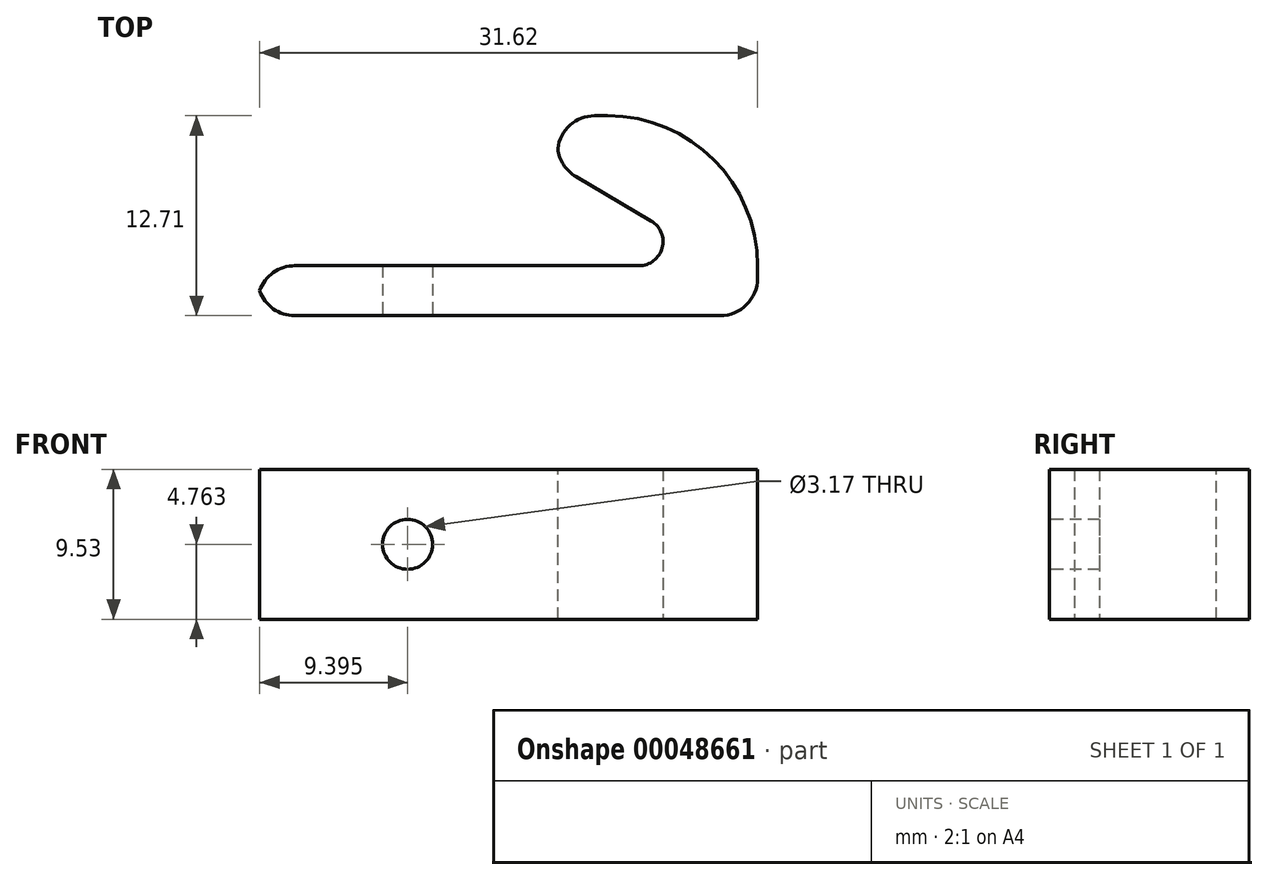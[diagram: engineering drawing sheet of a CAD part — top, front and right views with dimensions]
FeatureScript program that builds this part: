
annotation { "Feature Type Name" : "Feature", "Feature Type Description" : "" }
export const myFeature = defineFeature(function(context is Context, id is Id, definition is map)
    precondition{}
    {
        {
            var Q0;
            Q0=qCreatedBy(makeId("Top.planeOp"),FACE);
            var sketch = newSketch(context, id + "F0", { "sketchPlane" : qUnion([Q0])});
            skLineSegment(sketch, "E0.bottom", {"start": v(0, 0) * mm, "end": v(24.22, 0) * mm});
            skLineSegment(sketch, "E0.top", {"start": v(0, -3.18) * mm, "end": v(31.75, -3.18) * mm});
            skLineSegment(sketch, "E0.left", {"start": v(0, 0) * mm, "end": v(0, -3.18) * mm});
            skLineSegment(sketch, "E0.right", {"start": v(31.75, 0) * mm, "end": v(31.75, -3.18) * mm});
            skLineSegment(sketch, "E1.bottom", {"start": v(31.75, 0) * mm, "end": v(19.05, 3.17) * mm});
            skLineSegment(sketch, "E1.top", {"start": v(22.23, 9.52) * mm, "end": v(19.05, 9.52) * mm});
            skLineSegment(sketch, "E1.left", {"start": v(31.75, 0) * mm, "end": v(31.75, 0) * mm});
            skLineSegment(sketch, "E1.right", {"start": v(19.05, 6.35) * mm, "end": v(19.05, 9.52) * mm});
            skLineSegment(sketch, "E2", {"start": v(19.05, 6.35) * mm, "end": v(25, 2.84) * mm});
            skPoint(sketch, "E3.newPointA", {"position": v(31.75, 0) * mm});
            skPoint(sketch, "E3.newPointB", {"position": v(27, 1.65) * mm});
            skArc(sketch, "E3.filletArc", {"start": v(24.22, 0) * mm, "mid": v(25.7, 1.12) * mm, "end": v(25, 2.84) * mm});
            skPoint(sketch, "E4.visualSharp", {"position": v(31.75, 9.52) * mm});
            skArc(sketch, "E4.filletArc", {"start": v(31.75, 0) * mm, "mid": v(28.96, 6.74) * mm, "end": v(22.23, 9.52) * mm});
            skSolve(sketch);
        }
        {
            var Q0;
            Q0 = qSketchRegion(id + "F0", true);
            extrude(context, id + "F1", {"entities" : qUnion([Q0]), "depth" : 9.52 * mm});
        }
        {
            var Q0;
            Q0=makeQuery(id+"F1.opExtrude","SWEPT_FACE",FACE,{"disambiguationData":[OSD([sQuery(id+"F0.wireOp",EDGE,"E0.top")])]});
            var sketch = newSketch(context, id + "F2", { "sketchPlane" : qUnion([Q0])});
            skLineSegment(sketch, "E5", {"start": v(0, 4.76) * mm, "end": v(31.75, 4.76) * mm, "construction": true});
            skPoint(sketch, "E6", {"position": v(9.53, 4.76) * mm});
            skCircle(sketch, "E7", {"center": v(9.53, 4.76) * mm, "radius": 1.59 * mm});
            skSolve(sketch);
        }
        {
            var Q0;
            Q0 = qSketchRegion(id + "F2", true);
            extrude(context, id + "F3", {"entities" : qUnion([Q0]), "operationType" : NewBodyOperationType.REMOVE, "endBound" : BoundingType.THROUGH_ALL, "oppositeDirection" : true, "depth" : 25.4 * mm});
        }
        {
            var Q0;
            Q0=makeQuery(id+"F1.opExtrude","SWEPT_EDGE",EDGE,{"disambiguationData":[OSD([sQuery(id+"F0.wireOp",EDGE,"E0.top"),sQuery(id+"F0.wireOp",EDGE,"E0.right")])]});
            var Q1;
            Q1=makeQuery(id+"F1.opExtrude","SWEPT_EDGE",EDGE,{"disambiguationData":[OSD([sQuery(id+"F0.wireOp",EDGE,"E1.top"),sQuery(id+"F0.wireOp",EDGE,"E1.left")])]});
            var Q2;
            Q2=makeQuery(id+"F1.opExtrude","SWEPT_EDGE",EDGE,{"disambiguationData":[OSD([sQuery(id+"F0.wireOp",EDGE,"E1.top"),sQuery(id+"F0.wireOp",EDGE,"E1.right")])]});
            var Q3;
            Q3=makeQuery(id+"F1.opExtrude","SWEPT_EDGE",EDGE,{"disambiguationData":[OSD([sQuery(id+"F0.wireOp",EDGE,"E1.right"),sQuery(id+"F0.wireOp",EDGE,"E2")])]});
            var Q4;
            Q4=makeQuery(id+"F1.opExtrude","SWEPT_EDGE",EDGE,{"disambiguationData":[OSD([sQuery(id+"F0.wireOp",EDGE,"E0.top"),sQuery(id+"F0.wireOp",EDGE,"E0.left")])]});
            var Q5;
            Q5=makeQuery(id+"F1.opExtrude","SWEPT_EDGE",EDGE,{"disambiguationData":[OSD([sQuery(id+"F0.wireOp",EDGE,"E0.bottom"),sQuery(id+"F0.wireOp",EDGE,"E0.left")])]});
            fillet(context, id + "F4", {"entities" : qUnion([Q0, Q1, Q2, Q3, Q4, Q5]), "radius" : 2.36 * mm, "tangentPropagation" : true, "allowEdgeOverflow" : false});
        }
    });
